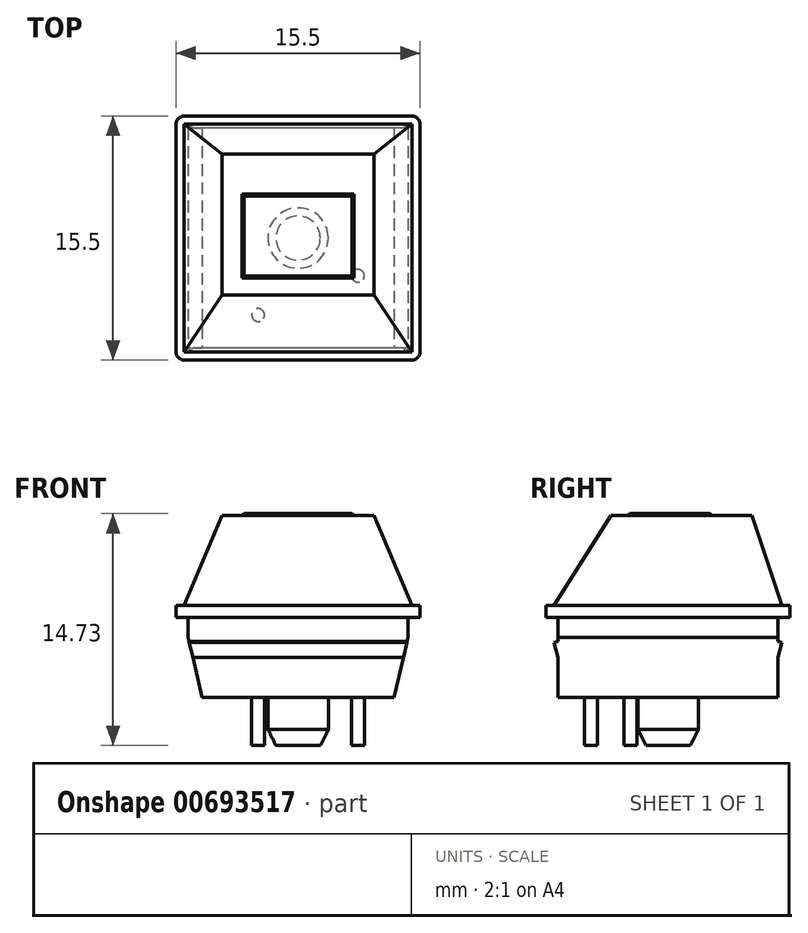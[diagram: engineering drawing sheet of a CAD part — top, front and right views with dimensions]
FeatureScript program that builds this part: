
annotation { "Feature Type Name" : "Feature", "Feature Type Description" : "" }
export const myFeature = defineFeature(function(context is Context, id is Id, definition is map)
    precondition{}
    {
        {
            var Q0;
            Q0=qCreatedBy(makeId("Top.planeOp"),FACE);
            var sketch = newSketch(context, id + "F0", { "sketchPlane" : qUnion([Q0])});
            skLineSegment(sketch, "E0.bottom", {"start": v(-7.24, 7.75) * mm, "end": v(7.24, 7.75) * mm});
            skLineSegment(sketch, "E0.top", {"start": v(-7.24, -7.75) * mm, "end": v(7.24, -7.75) * mm});
            skLineSegment(sketch, "E0.left", {"start": v(-7.75, 7.24) * mm, "end": v(-7.75, -7.24) * mm});
            skLineSegment(sketch, "E0.right", {"start": v(7.75, 7.24) * mm, "end": v(7.75, -7.24) * mm});
            skPoint(sketch, "E1", {"position": v(0, 7.75) * mm});
            skPoint(sketch, "E2", {"position": v(-7.75, 0) * mm});
            skPoint(sketch, "E3.visualSharp", {"position": v(-7.75, 7.75) * mm});
            skArc(sketch, "E3.filletArc", {"start": v(-7.24, 7.75) * mm, "mid": v(-7.6, 7.6) * mm, "end": v(-7.75, 7.24) * mm});
            skPoint(sketch, "E4.visualSharp", {"position": v(7.75, 7.75) * mm});
            skArc(sketch, "E4.filletArc", {"start": v(7.75, 7.24) * mm, "mid": v(7.6, 7.6) * mm, "end": v(7.24, 7.75) * mm});
            skPoint(sketch, "E5.visualSharp", {"position": v(7.75, -7.75) * mm});
            skArc(sketch, "E5.filletArc", {"start": v(7.24, -7.75) * mm, "mid": v(7.6, -7.6) * mm, "end": v(7.75, -7.24) * mm});
            skPoint(sketch, "E6.visualSharp", {"position": v(-7.75, -7.75) * mm});
            skArc(sketch, "E6.filletArc", {"start": v(-7.75, -7.24) * mm, "mid": v(-7.6, -7.6) * mm, "end": v(-7.24, -7.75) * mm});
            skSolve(sketch);
        }
        {
            var Q0;
            Q0=qSketchRegion(id+"F0",true);
            extrude(context, id + "F1", {"entities" : qUnion([Q0]), "depth" : 11.68 * mm});
        }
        {
            var Q0;
            Q0=makeQuery(id+"F1.opExtrude","SWEPT_FACE",FACE,{"disambiguationData":[OSD([sQuery(id+"F0.wireOp",EDGE,"E0.top")])]});
            var sketch = newSketch(context, id + "F2", { "sketchPlane" : qUnion([Q0])});
            skLineSegment(sketch, "E7", {"start": v(-3.43, 11.68) * mm, "end": v(-3.56, 11.56) * mm});
            skLineSegment(sketch, "E8", {"start": v(-3.56, 11.56) * mm, "end": v(-4.83, 11.56) * mm});
            skLineSegment(sketch, "E9", {"start": v(-4.83, 11.56) * mm, "end": v(-7.24, 5.84) * mm});
            skLineSegment(sketch, "E10", {"start": v(-7.24, 5.84) * mm, "end": v(-7.75, 5.84) * mm});
            skLineSegment(sketch, "E11", {"start": v(-7.75, 5.84) * mm, "end": v(-7.75, 11.68) * mm});
            skLineSegment(sketch, "E12", {"start": v(-7.75, 11.68) * mm, "end": v(-3.43, 11.68) * mm});
            skLineSegment(sketch, "E13", {"start": v(-7.75, 5.08) * mm, "end": v(-6.99, 5.08) * mm});
            skLineSegment(sketch, "E14", {"start": v(-6.98, 5.08) * mm, "end": v(-6.98, 3.81) * mm});
            skLineSegment(sketch, "E15", {"start": v(-6.99, 3.81) * mm, "end": v(-6.1, 0) * mm});
            skLineSegment(sketch, "E16", {"start": v(-6.1, 0) * mm, "end": v(-7.75, 0) * mm});
            skLineSegment(sketch, "E17", {"start": v(-7.75, 0) * mm, "end": v(-7.75, 5.08) * mm});
            skLineSegment(sketch, "E18", {"start": v(0, 11.68) * mm, "end": v(0, 0) * mm, "construction": true});
            skLineSegment(sketch, "E19.0.MirrorCS", {"start": v(3.43, 11.68) * mm, "end": v(3.56, 11.56) * mm});
            skLineSegment(sketch, "E19.1.MirrorCS", {"start": v(6.99, 5.08) * mm, "end": v(6.99, 3.81) * mm});
            skLineSegment(sketch, "E19.2.MirrorCS", {"start": v(3.56, 11.56) * mm, "end": v(4.83, 11.56) * mm});
            skLineSegment(sketch, "E19.3.MirrorCS", {"start": v(6.99, 3.81) * mm, "end": v(6.1, 0) * mm});
            skLineSegment(sketch, "E19.4.MirrorCS", {"start": v(4.83, 11.56) * mm, "end": v(7.24, 5.84) * mm});
            skLineSegment(sketch, "E19.5.MirrorCS", {"start": v(6.1, 0) * mm, "end": v(7.75, 0) * mm});
            skLineSegment(sketch, "E19.6.MirrorCS", {"start": v(7.24, 5.84) * mm, "end": v(7.75, 5.84) * mm});
            skLineSegment(sketch, "E19.7.MirrorCS", {"start": v(7.75, 0) * mm, "end": v(7.75, 5.08) * mm});
            skLineSegment(sketch, "E19.8.MirrorCS", {"start": v(7.75, 5.08) * mm, "end": v(6.99, 5.08) * mm});
            skLineSegment(sketch, "E19.9.MirrorCS", {"start": v(7.75, 5.84) * mm, "end": v(7.75, 11.68) * mm});
            skLineSegment(sketch, "E19.10.MirrorCS", {"start": v(7.75, 11.68) * mm, "end": v(3.43, 11.68) * mm});
            skSolve(sketch);
        }
        {
            var Q0;
            Q0=qSketchRegion(id+"F2",true);
            extrude(context, id + "F3", {"entities" : qUnion([Q0]), "operationType" : NewBodyOperationType.REMOVE, "endBound" : BoundingType.THROUGH_ALL, "oppositeDirection" : true, "depth" : 25.4 * mm});
        }
        {
            var Q0;
            Q0=makeQuery(id+"F1.opExtrude","SWEPT_FACE",FACE,{"disambiguationData":[OSD([sQuery(id+"F0.wireOp",EDGE,"E0.left")])]});
            var sketch = newSketch(context, id + "F4", { "sketchPlane" : qUnion([Q0])});
            skLineSegment(sketch, "E20", {"start": v(-7.75, 5.08) * mm, "end": v(-6.99, 5.08) * mm});
            skLineSegment(sketch, "E21", {"start": v(-6.99, 5.08) * mm, "end": v(-6.99, 3.56) * mm});
            skLineSegment(sketch, "E22", {"start": v(-6.99, 2.54) * mm, "end": v(-6.99, 0) * mm});
            skLineSegment(sketch, "E23", {"start": v(-6.99, 0) * mm, "end": v(-7.75, 0) * mm});
            skLineSegment(sketch, "E24", {"start": v(-7.75, 0) * mm, "end": v(-7.75, 5.08) * mm});
            skPoint(sketch, "E25", {"position": v(-6.99, 2.54) * mm});
            skLineSegment(sketch, "E26", {"start": v(-6.99, 3.56) * mm, "end": v(-7.24, 3.49) * mm});
            skLineSegment(sketch, "E27", {"start": v(-7.24, 3.49) * mm, "end": v(-6.99, 2.54) * mm});
            skLineSegment(sketch, "E28", {"start": v(0, 0) * mm, "end": v(0, 2.67) * mm, "construction": true});
            skLineSegment(sketch, "E29.0.MirrorCS", {"start": v(6.99, 3.56) * mm, "end": v(7.24, 3.49) * mm});
            skLineSegment(sketch, "E29.1.MirrorCS", {"start": v(7.75, 5.08) * mm, "end": v(6.99, 5.08) * mm});
            skLineSegment(sketch, "E29.2.MirrorCS", {"start": v(6.99, 0) * mm, "end": v(7.75, 0) * mm});
            skPoint(sketch, "E29.3.MirrorP", {"position": v(6.99, 2.54) * mm});
            skLineSegment(sketch, "E29.4.MirrorCS", {"start": v(7.75, 0) * mm, "end": v(7.75, 5.08) * mm});
            skLineSegment(sketch, "E29.5.MirrorCS", {"start": v(6.99, 2.54) * mm, "end": v(6.99, 0) * mm});
            skLineSegment(sketch, "E29.6.MirrorCS", {"start": v(6.99, 5.08) * mm, "end": v(6.99, 3.56) * mm});
            skLineSegment(sketch, "E29.7.MirrorCS", {"start": v(7.24, 3.49) * mm, "end": v(6.99, 2.54) * mm});
            skLineSegment(sketch, "E30", {"start": v(-7.75, 5.84) * mm, "end": v(-7.24, 5.84) * mm});
            skLineSegment(sketch, "E31", {"start": v(-7.24, 5.84) * mm, "end": v(-5.33, 11.56) * mm});
            skLineSegment(sketch, "E32", {"start": v(-5.33, 11.56) * mm, "end": v(-2.8, 11.56) * mm});
            skLineSegment(sketch, "E33", {"start": v(-2.8, 11.56) * mm, "end": v(-2.67, 11.68) * mm});
            skLineSegment(sketch, "E34", {"start": v(-2.67, 11.68) * mm, "end": v(-7.75, 11.68) * mm});
            skLineSegment(sketch, "E35", {"start": v(-7.75, 11.68) * mm, "end": v(-7.75, 5.84) * mm});
            skLineSegment(sketch, "E36", {"start": v(7.75, 5.84) * mm, "end": v(7.24, 5.84) * mm});
            skLineSegment(sketch, "E37", {"start": v(7.24, 5.84) * mm, "end": v(3.63, 11.56) * mm});
            skLineSegment(sketch, "E38", {"start": v(3.63, 11.56) * mm, "end": v(2.54, 11.56) * mm});
            skLineSegment(sketch, "E39", {"start": v(2.54, 11.56) * mm, "end": v(2.41, 11.68) * mm});
            skLineSegment(sketch, "E40", {"start": v(2.41, 11.68) * mm, "end": v(7.75, 11.68) * mm});
            skLineSegment(sketch, "E41", {"start": v(7.75, 11.68) * mm, "end": v(7.75, 5.84) * mm});
            skSolve(sketch);
        }
        {
            var Q0;
            Q0=qSketchRegion(id+"F4",true);
            extrude(context, id + "F5", {"entities" : qUnion([Q0]), "operationType" : NewBodyOperationType.REMOVE, "endBound" : BoundingType.THROUGH_ALL, "oppositeDirection" : true, "depth" : 25.4 * mm});
        }
        {
            var Q0;
            Q0=makeQuery(id+"F1.opExtrude","CAP_FACE",FACE,{"disambiguationData":[OSD([sQuery(id+"F0.wireOp",EDGE,"E0.bottom"),sQuery(id+"F0.wireOp",EDGE,"E0.top"),sQuery(id+"F0.wireOp",EDGE,"E0.left"),sQuery(id+"F0.wireOp",EDGE,"E0.right"),sQuery(id+"F0.wireOp",EDGE,"E3.filletArc"),sQuery(id+"F0.wireOp",EDGE,"E4.filletArc"),sQuery(id+"F0.wireOp",EDGE,"E5.filletArc"),sQuery(id+"F0.wireOp",EDGE,"E6.filletArc")])],"isStart":true});
            var sketch = newSketch(context, id + "F6", { "sketchPlane" : qUnion([Q0])});
            skCircle(sketch, "E42", {"center": v(0, 0) * mm, "radius": 1.92 * mm});
            skCircle(sketch, "E43", {"center": v(3.8, 2.4) * mm, "radius": 0.4 * mm});
            skCircle(sketch, "E44", {"center": v(-2.54, 4.89) * mm, "radius": 0.4 * mm});
            skSolve(sketch);
        }
        {
            var Q0;
            Q0=qSketchRegion(id+"F6",true);
            extrude(context, id + "F7", {"entities" : qUnion([Q0]), "operationType" : NewBodyOperationType.ADD, "depth" : 3.05 * mm});
        }
        {
            var Q0;
            Q0=makeQuery(id+"F7.opExtrude","CAP_FACE",FACE,{"disambiguationData":[OSD([sQuery(id+"F6.wireOp",EDGE,"E42")])],"isStart":false});
            chamfer(context, id + "F8", {"entities" : qUnion([Q0]), "chamferType" : ChamferType.TWO_OFFSETS, "width1" : 0.5 * mm, "oppositeDirection" : false, "width2" : 1.02 * mm, "tangentPropagation" : true});
        }
    });
